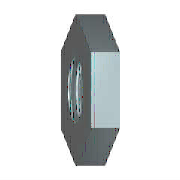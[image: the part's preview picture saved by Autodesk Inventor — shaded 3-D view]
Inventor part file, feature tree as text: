
AUTODESK INVENTOR PART (.ipt)
format: ipt  version: 2022 (Build 260153000, 153)  size: 136,192 bytes
history: native  units: mm (DEFAULTED — no unit token found)
features: other x4, sketch x2
ambient origin geometry x8: Origin, YZ Plane, XZ Plane, XY Plane, X Axis, Y Axis, Z Axis, Center Point
bodies: Solid1 (feature_tree)
feature tree (6):
  other  "MSC_A1"
  other  "MSC_PT1"
  other  "MSC_PT2"
  other  "MSC_PF1"
  sketch  "Boceto1"  dims[d2=0.0mm]
  sketch  "Boceto2"  dims[d3=1.567mm d4=1.2mm d5=4.0mm d6=2.0mm d7=60.0deg d8=8.0mm d9=20.594885mm d14=0.0mm d15=0.0mm d16=0.0mm d17=0.24mm d18=0.24mm d20=45.0deg d21=0.0mm d23=0.0mm d24=0.0mm d25=0.0mm]
